# Revit family: LMEZ-VL
name_source: partatom
category: Lighting Fixtures
units: mm (PartAtom-declared; Revit-internal decimal feet)

## family parameters
Always vertical = Yes
Cut with Voids When Loaded = No
Host = Ceiling
Light Source = Yes
OmniClass Number = 23.80.70.11.14.17
OmniClass Title = Direct/Indirect
Part Type = Normal
Room Calculation Point = No
Round Connector Dimension = Use Diameter
Shared = No

## types (4) — shared parameters
Assembly Code = D5020200
Color Filter = 16777215
Description = LED MEZ VL
Dimming Lamp Color Temperature Shift = <None>
Height = 0' - 4 17/32"
Housing Finish = Metal - Viscor - White
Lamp = LED
Lens Finsih = Polycarbonate - Viscor - Frosted
Manufacturer = VISIONEERING by VISCOR
Model = LMEZ-VL
Tilt Angle = 90.00°
URL = https://www.viscor.com
Voltage = 120 V
Width = 0' - 3 1/8"

## per-type parameters (varying)
| type | Apparent Load | Emit from Line Length | Lamp Wattage | Length | Photometric Web File |
| LMEZ-VL48-LED840K040LUNV | 29 VA | 3' - 8 15/32" | 29 VA | 3' - 8 15/32" | LMEZ-VL48-LED840K040LUNV-G002667.IES |
| LMEZ-VLD48-LED840K030LUNV | 30 VA | 3' - 8 15/32" | 30 VA | 3' - 8 15/32" | LMEZ-VLD48-LED840K030LUNV-G002517.IES |
| LMEZ-VLD96-LED840K060LUNV | 57 VA | 7' - 4 23/32" | 57 VA | 7' - 4 23/32" | LMEZ-VLD96-LED840K060LUNV.ies |
| LMEZ-VL96-LED840K080LUNV | 63 VA | 7' - 4 23/32" | 63 VA | 7' - 4 23/32" | LMEZ-VL96-LED840K080LUNV.ies |

## geometry (parser evidence)
native form markers: Sweep x3
no freeform markers — native parametric forms only
